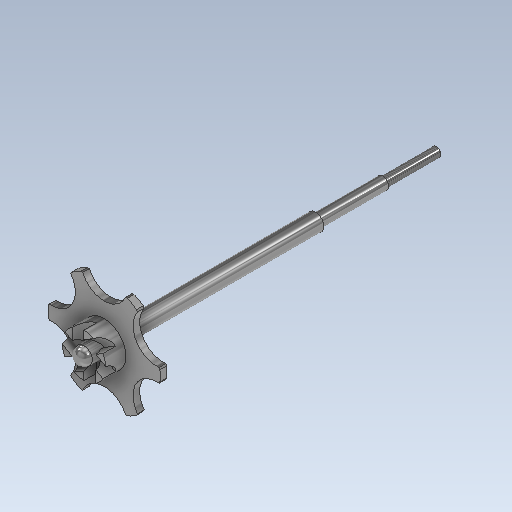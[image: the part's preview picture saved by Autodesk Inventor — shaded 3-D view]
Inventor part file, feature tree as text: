
AUTODESK INVENTOR PART (.ipt)
format: ipt  version: 2021 (Build 250183000, 183)  size: 304,128 bytes
history: native  units: mm
features: sketch x17, extrude x15, other x10, pattern_circular x5, thread x1
ambient origin geometry x8: Origin, YZ Plane, XZ Plane, XY Plane, X Axis, Y Axis, Z Axis, Center Point
bodies: Body1 (feature_tree)
feature tree (48):
  other  "Sólido1"
  extrude  "Extrusão1"  Depth=33.0mm TaperAngle=0.0deg
  sketch  "Esboço2"  dims[d3=6.5mm d4=7.0mm]
  extrude  "Extrusão2"  Depth=7.0mm
  pattern_circular  "Padrão circular1"  Count=6 Angle=360.0deg
  extrude  "Extrusão3"  Depth=0.5mm
  sketch  "Esboço6"  dims[d11=6.5mm d12=0.5mm]
  other  "Ponto de trabalho1"
  other  "Revolução1"
  pattern_circular  "Padrão circular2"  Count=6 Angle=360.0deg
  other  "Plano de trabalho2"
  extrude  "Extrusão4"  Depth=7.5mm
  pattern_circular  "Padrão circular3"  Count=6 Angle=360.0deg
  extrude  "Extrusão5"  Depth=3.25mm
  other  "Plano de trabalho3"
  extrude  "Extrusão6"  Depth=2.191261mm
  pattern_circular  "Padrão circular4"  Count=6 Angle=360.0deg
  extrude  "Extrusão7"  TaperAngle=0.0deg  [1 undecoded]
  extrude  "Extrusão8"  TaperAngle=0.0deg  [1 undecoded]
  other  "Plano de trabalho4"
  extrude  "Extrusão9"  [1 undecoded]
  other  "Plano de trabalho5"
  sketch  "Esboço12"  dims[d23=1.0mm d24=0.0mm d25=60.0mm d26=360.0deg]
  other  "Eixo de trabalho4"
  other  "Revolução2"
  extrude  "Extrusão10"  Depth=1.0mm
  extrude  "Extrusão11"  TaperAngle=0.0deg  [1 undecoded]
  extrude  "Extrusão12"  Depth=3.0mm
  extrude  "Extrusão13"  TaperAngle=90.0deg  [1 undecoded]
  thread  "Rosca1"  [1 undecoded]
  extrude  "Extrusão14"  Depth=1.0mm
  extrude  "Extrusão15"  Depth=4.3mm
  pattern_circular  "Padrão circular5"  [2 undecoded]
  sketch  "Esboço1"  dims[d0=26.0mm d1=33.0mm d2=0.0mm]
  sketch  "Esboço3"  dims[d5=8.0mm]
  sketch  "Esboço4"  dims[d6=0.0mm d7=0.0mm d8=60.0mm d9=360.0deg]
  other  "Contorno projetado1"
  sketch  "Esboço7"  dims[d13=22.0mm d14=0.0mm]
  sketch  "Esboço8"  dims[d15=90.0deg d16=60.0mm d17=360.0deg]
  sketch  "Esboço9"  dims[d19=13.0mm d20=7.5mm]
  sketch  "Esboço10"  dims[d21=3.5mm]
  sketch  "Esboço11"  dims[d22=4.0mm]
  sketch  "Esboço13"  dims[d28=3.0mm d29=0.0mm d30=3.25mm]
  sketch  "Esboço14"  dims[d33=3.281864mm d34=2.191261mm]
  sketch  "Esboço15"  dims[d35=0.408292mm]
  sketch  "Esboço16"  dims[d36=3.0mm d37=0.0mm d38=60.0mm d39=360.0deg]
  sketch  "Esboço17"  dims[d41=2.5mm d42=0.0mm d43=0.0mm]
  sketch  "Esboço18"  dims[d44=16.7mm d45=0.0mm d46=0.0mm d47=-1.0mm d48=16.7mm d49=0.0mm d50=0.0mm d51=3.0mm d52=90.0deg d53=40.5mm d54=4.0mm d55=0.0mm d56=0.0mm d57=0.5mm d58=4.3mm d59=0.0mm d60=0.0mm d61=1.8mm d62=2.5mm d63=10.0mm d64=0.0mm d65=1.4mm d66=8.0mm d67=0.0mm d68=15.255mm d69=0.0mm d70=1.0mm d71=0.0mm d73=7.0mm d74=9.0mm d75=1.0mm d76=0.0mm d77=60.0mm d78=360.0deg]
note: 8 required parameter values undecoded (feature->parameter linkage not recoverable at this tier; creation-order binding heuristic only, values carry confidence <= 0.55)
